annotation { "Feature Type Name" : "Feature", "Feature Type Description" : "" }
export const myFeature = defineFeature(function(context is Context, id is Id, definition is map)
    precondition{}
    {
        {
            var Q0;
            Q0=qCreatedBy(makeId("Top.planeOp"),FACE);
            var sketch = newSketch(context, id + "F0", { "sketchPlane" : qUnion([Q0])});
            skLineSegment(sketch, "E0.bottom", {"start": v(193.23, 85.56) * mm, "end": v(-193.23, 85.56) * mm});
            skLineSegment(sketch, "E0.top", {"start": v(193.23, -85.56) * mm, "end": v(-193.23, -85.56) * mm});
            skLineSegment(sketch, "E0.left", {"start": v(193.23, 85.56) * mm, "end": v(193.23, -85.56) * mm});
            skLineSegment(sketch, "E0.right", {"start": v(-193.23, 85.56) * mm, "end": v(-193.23, -85.56) * mm});
            skPoint(sketch, "E0.middle", {"position": v(0, 0) * mm});
            skText(sketch, "E1", { "text": "Trustworthy  Loyal  Helpful  Friendly Courteous Kind", "fontName": "NotoSansCJKjp-Bold.otf"});
            skText(sketch, "E2", { "text": "Obedient  Cheerful  Thrifty  Brave  Clean  Reverent", "fontName": "OpenSans-Bold.ttf"});
            skText(sketch, "E3", { "text": "Samuel Gunter", "fontName": "OpenSans-Bold.ttf"});
            skLineSegment(sketch, "E4.bottom", {"start": v(-144.25, -32.92) * mm, "end": v(-138.24, -32.92) * mm});
            skLineSegment(sketch, "E4.top", {"start": v(-144.25, -29.92) * mm, "end": v(-138.24, -29.92) * mm});
            skLineSegment(sketch, "E4.left", {"start": v(-144.25, -32.92) * mm, "end": v(-144.25, -29.92) * mm});
            skPoint(sketch, "E4.middle", {"position": v(0, -31.42) * mm});
            skLineSegment(sketch, "E5", {"start": v(144.25, -29.92) * mm, "end": v(121.36, -19.8) * mm});
            skLineSegment(sketch, "E6", {"start": v(121.36, -19.8) * mm, "end": v(121.36, -29.92) * mm});
            skLineSegment(sketch, "E7", {"start": v(121.36, -41.97) * mm, "end": v(144.25, -32.92) * mm});
            skLineSegment(sketch, "E8", {"start": v(144.25, -31.42) * mm, "end": v(148.8, -31.42) * mm, "construction": true});
            skPoint(sketch, "E8.endSnap0", {"position": v(144.25, -31.42) * mm});
            skLineSegment(sketch, "E9", {"start": v(144.25, -32.92) * mm, "end": v(147.45, -31.42) * mm});
            skLineSegment(sketch, "E10", {"start": v(147.45, -31.42) * mm, "end": v(144.25, -29.92) * mm});
            skLineSegment(sketch, "E11.trimOffspring", {"start": v(121.36, -32.92) * mm, "end": v(121.36, -41.97) * mm});
            skLineSegment(sketch, "E12", {"start": v(-138.24, -29.92) * mm, "end": v(-146.82, -19.21) * mm});
            skLineSegment(sketch, "E13", {"start": v(-146.82, -19.21) * mm, "end": v(-121.94, -19.21) * mm});
            skLineSegment(sketch, "E14", {"start": v(-121.94, -19.21) * mm, "end": v(-113.35, -29.92) * mm});
            skLineSegment(sketch, "E15", {"start": v(-144.25, -31.42) * mm, "end": v(-111.07, -31.42) * mm, "construction": true});
            skLineSegment(sketch, "E16.MirrorCS", {"start": v(-138.24, -32.92) * mm, "end": v(-146.82, -43.64) * mm});
            skLineSegment(sketch, "E17.MirrorCS", {"start": v(-146.82, -43.64) * mm, "end": v(-121.94, -43.64) * mm});
            skLineSegment(sketch, "E18.MirrorCS", {"start": v(-121.94, -43.64) * mm, "end": v(-113.35, -32.92) * mm});
            skLineSegment(sketch, "E19.trimOffspring", {"start": v(-113.35, -29.92) * mm, "end": v(121.36, -29.92) * mm});
            skLineSegment(sketch, "E20.trimOffspring", {"start": v(-113.35, -32.92) * mm, "end": v(121.36, -32.92) * mm});
            skLineSegment(sketch, "E21.bottom", {"start": v(-198.7, 90.02) * mm, "end": v(199.1, 90.02) * mm});
            skLineSegment(sketch, "E21.top", {"start": v(-198.7, -89.67) * mm, "end": v(199.1, -89.67) * mm});
            skLineSegment(sketch, "E21.left", {"start": v(-198.7, 90.02) * mm, "end": v(-198.7, -89.67) * mm});
            skLineSegment(sketch, "E21.right", {"start": v(199.1, 90.02) * mm, "end": v(199.1, -89.67) * mm});
            const initialGuessF0  = {"E1": [-0.18283, 0.06102, 1, 0, 0.0101], "E2": [-0.17706, -0.07198, 1, 0, 0.0101], "E3": [-0.11625, 0, 1, 0, 0.02158]};
            skSetInitialGuess(sketch, initialGuessF0);
            skSolve(sketch);
        }
        {
            var Q0;
            Q0=makeQuery(id+"F0.imprint","IMPRINT",FACE,{"disambiguationData":[TD([[makeQuery(id+"F0.imprint","IMPRINT",EDGE,{"derivedFrom":sQuery(id+"F0.wireOp",EDGE,"E0.bottom")}),1.0]])]});
            extrude(context, id + "F1", {"entities" : qUnion([Q0]), "depth" : 2 * mm});
        }
        {
            var Q0;
            Q0=makeQuery(id+"F0.imprint","IMPRINT",FACE,{"disambiguationData":[TD([[makeQuery(id+"F0.imprint","IMPRINT",EDGE,{"derivedFrom":sQuery(id+"F0.wireOp",EDGE,"E0.bottom")}),-1.0]])]});
            extrude(context, id + "F2", {"entities" : qUnion([Q0]), "operationType" : NewBodyOperationType.ADD, "depth" : 4 * mm});
        }
    });